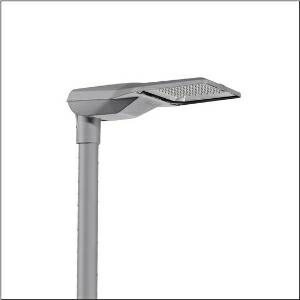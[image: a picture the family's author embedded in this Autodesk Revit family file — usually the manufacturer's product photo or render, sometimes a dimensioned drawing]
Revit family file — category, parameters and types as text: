
# Revit family: streetlight_sl_21_iq_midi___st0_5a_5xe3b31g08mb_2812
name_source: partatom
category: Lighting Fixtures
units: mm (PartAtom-declared; Revit-internal decimal feet)

## family parameters
Cut with Voids When Loaded = No
Host = Face
Light Source = No
Part Type = Normal
Room Calculation Point = No
Round Connector Dimension = Use Diameter
Shared = No

## types (1)
- --- (1 x LED, 19500 lm, 146.7 W, 3000K)
    Apparent Load = 147 VA
    CIE Flux Codes = 41 75 97 100 100
    Color Rendering = 70
    Color Temperature = 3000K
    Default Elevation = 1800 mm
    Description = Streetlight SL 21 iQ midi, mast luminaire, primary light control with lens, of PMMA, primary optical cover: cover, of toughened safety glass, transparent, light distribution: ST0.5a, light emission: direct distribution, primary light characteristic: asymmetric, installation type: post-top, side-entry, LED, High Power LED, rated luminous flux: 19.500lm, luminous efficacy: 133lm/W, light colour: 730, colour temperature: 3000K, control gear: iQ Street-Remote, control: Street-Remote, Auto-Match, Temp-Guard, Lumen-Switch, Night-Set, Smart-Wire, Light-Fading, Desk-Remote (wireless, voltage-free reading and setting of iQ features in the workshop via application-optimized NFC function/RFID function), optimised constant luminous flux control (CLO 2.0), pre-setting: linear dimming characteristic, mains connection: 230..240V, AC, 50/60Hz, start of lifetime: 147W, end of service life: 161W, reduction: 62W, luminaire housing, of diecast aluminium, powder-coated, Siteco® metallic grey (DB 702S), corrosivity category C5 mid according to DIN EN ISO 12944, please order mast flange separately, inclination adjustable: 0°, 5°, 10°, 15°, sealing non-destructively replaceable, multi-level sealing system, length: 644mm, width: 335mm, height: 110mm, mast flange for spigot size: 42mm (side-entry): 5XC10008XM4, 60/48mm (side-entry/post-top): 5XC10108XM2, 76/60mm (side-entry/post-top): 5XC10108XM1, mounting height: 4..8m, protection rating (complete): IP66, insulation class (complete): insulation class II (safety insulation), certification: CE, ENEC, ENEC+, VDE, impact resistance: IK10, permissible operating ambient temperature for outdoor applications: -40..+50°C, standard-compliant lighting for roads and squares, packaging unit: 1 piece

Light Distribution: ST0.5a
    Height = 111 mm
    Lamp = 1 x LED
    Lamp Light Flux = 19500 lm
    Lamp Power = 146.7 W
    Lamp count = 1
    Length = 644 mm
    Luminous efficacy = 133 lm/W
    Manufacturer = Siteco
    ModVariant = No
    Model = 5XE3B31G08MB
    Number of Poles = 1
    OnlyDefault = Yes
    Power Factor = 1
    Product Name = Streetlight SL 21 iQ midi | ST0.5a
    Product group = mast luminaire | pylon top
    ProductGroupID = 6100
    Protection Class = Protection class II
    Protection Degree = IP 66
    RLX_Detail_Level = 1
    RLX_Emergency_Light_Flux = 0 lm
    RLX_Emergency_Type = 0
    RLX_Emergency_Type_DB = No
    RlxData = <blob elided: 37929 chars, md5=710967b3>
    Socket = socket
    Standby Power = 0 W
    System Light Flux = 19499 lm
    System Power = 147 W
    Type Comments = factory setting: luminous flux: 100 % | dim-lin: 254 | 753 mA
    Type Image = l_1004298.jpg
    URL = http://relux.com
    VarID = @adj_191834
    Voltage = 0 V
    Weight = 0.00 kg
    Width = 336 mm

## geometry (parser evidence)
native form markers: Blend x4, Sweep x9
no freeform markers — native parametric forms only
